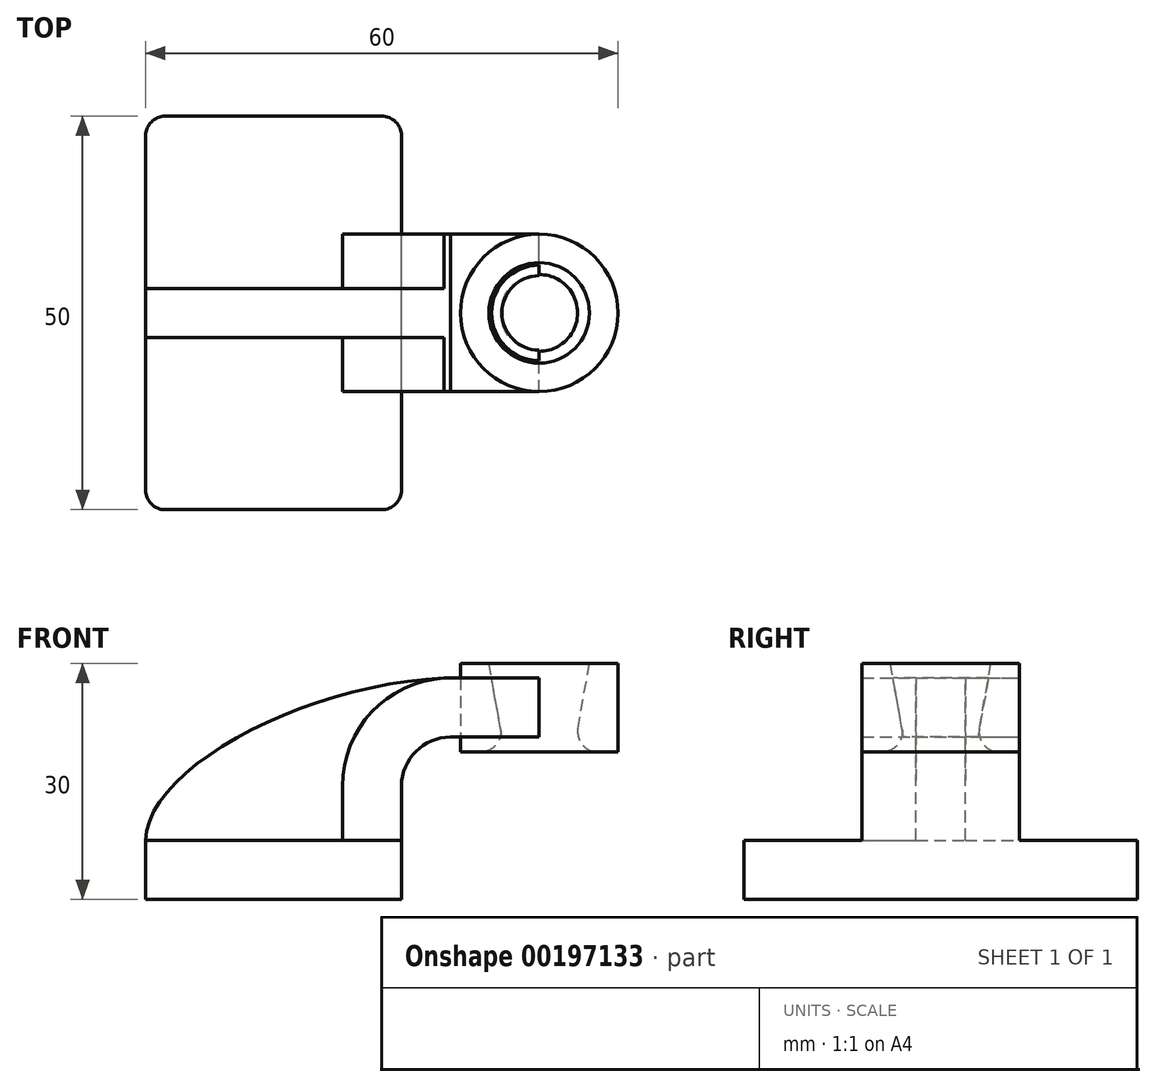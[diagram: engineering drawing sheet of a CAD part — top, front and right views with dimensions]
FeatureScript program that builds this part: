
annotation { "Feature Type Name" : "Feature", "Feature Type Description" : "" }
export const myFeature = defineFeature(function(context is Context, id is Id, definition is map)
    precondition{}
    {
        {
            var Q0;
            Q0=qCreatedBy(makeId("Front.planeOp"),FACE);
            var sketch = newSketch(context, id + "F0", { "sketchPlane" : qUnion([Q0])});
            skLineSegment(sketch, "E0.bottom", {"start": v(16.25, 3.75) * mm, "end": v(-16.25, 3.75) * mm});
            skLineSegment(sketch, "E0.top", {"start": v(16.25, -3.75) * mm, "end": v(-16.25, -3.75) * mm});
            skLineSegment(sketch, "E0.left", {"start": v(16.25, 3.75) * mm, "end": v(16.25, -3.75) * mm});
            skLineSegment(sketch, "E0.right", {"start": v(-16.25, 3.75) * mm, "end": v(-16.25, -3.75) * mm});
            skPoint(sketch, "E0.middle", {"position": v(0, 0) * mm});
            skLineSegment(sketch, "E1.bottom", {"start": v(43.75, 15) * mm, "end": v(23.75, 15) * mm});
            skLineSegment(sketch, "E1.top", {"start": v(43.75, 26.25) * mm, "end": v(23.75, 26.25) * mm});
            skLineSegment(sketch, "E1.left", {"start": v(43.75, 15) * mm, "end": v(43.75, 26.25) * mm});
            skLineSegment(sketch, "E1.right", {"start": v(23.75, 15) * mm, "end": v(23.75, 26.25) * mm});
            skPoint(sketch, "E1.middle", {"position": v(33.75, 20.63) * mm});
            skLineSegment(sketch, "E2", {"start": v(16.25, 3.75) * mm, "end": v(16.25, 10.63) * mm});
            skArc(sketch, "E3", {"start": v(16.25, 10.63) * mm, "mid": v(18.08, 15.05) * mm, "end": v(22.5, 16.88) * mm});
            skLineSegment(sketch, "E4", {"start": v(22.5, 16.88) * mm, "end": v(33.75, 16.88) * mm});
            skLineSegment(sketch, "E5.0", {"start": v(22.5, 24.38) * mm, "end": v(33.75, 24.38) * mm});
            skArc(sketch, "E5.1", {"start": v(8.75, 10.63) * mm, "mid": v(12.78, 20.35) * mm, "end": v(22.5, 24.38) * mm});
            skLineSegment(sketch, "E5.2", {"start": v(8.75, 3.75) * mm, "end": v(8.75, 10.63) * mm});
            skLineSegment(sketch, "E6", {"start": v(33.75, 15) * mm, "end": v(33.75, 26.25) * mm});
            skFitSpline(sketch, "E7", {"points": [v(-16.25, 3.75) * mm, v(22.5, 24.38) * mm], "startDerivative": vector(0.42, 28.18) * mm, "endDerivative": vector(52.82, 1.15) * mm});
            skSolve(sketch);
        }
        {
            var Q0;
            Q0=makeQuery(id+"F0.imprint","IMPRINT",FACE,{"disambiguationData":[TD([[makeQuery(id+"F0.imprint","IMPRINT",EDGE,{"derivedFrom":sQuery(id+"F0.wireOp",EDGE,"E0.top")}),-1.0]])]});
            extrude(context, id + "F1", {"entities" : qUnion([Q0]), "endBound" : BoundingType.SYMMETRIC, "depth" : 50 * mm});
        }
        {
            var Q0;
            {var subQ1=sQuery(id+"F0.wireOp",EDGE,"E2");Q0=makeQuery(id+"F0.imprint","IMPRINT",FACE,{"disambiguationData":[TD([[makeQuery(id+"F0.imprint","IMPRINT",EDGE,{"derivedFrom":subQ1}),1.0]])]});}
            var Q1;
            {var subQ0=sQuery(id+"F0.wireOp",EDGE,"E4");var subQ1=sQuery(id+"F0.wireOp",EDGE,"E1.right");var subQ2=makeQuery(id+"F0.imprint","INTERSECT",VERTEX,{"derivedFrom":[subQ1,subQ0]});Q1=makeQuery(id+"F0.imprint","IMPRINT",FACE,{"disambiguationData":[TD([[makeQuery(id+"F0.imprint","IMPRINT",EDGE,{"disambiguationData":[TD([[subQ2,-1.0]])],"derivedFrom":subQ1}),-1.0]])]});}
            extrude(context, id + "F2", {"entities" : qUnion([Q0, Q1]), "operationType" : NewBodyOperationType.ADD, "endBound" : BoundingType.SYMMETRIC, "depth" : 20 * mm});
        }
        {
            var Q0;
            {var subQ3=sQuery(id+"F0.wireOp",EDGE,"E5.2");Q0=makeQuery(id+"F0.imprint","IMPRINT",FACE,{"disambiguationData":[TD([[makeQuery(id+"F0.imprint","IMPRINT",EDGE,{"derivedFrom":subQ3}),1.0]])]});}
            extrude(context, id + "F3", {"entities" : qUnion([Q0]), "operationType" : NewBodyOperationType.ADD, "endBound" : BoundingType.SYMMETRIC, "depth" : 6.25 * mm});
        }
        {
            var Q0;
            {var subQ0=sQuery(id+"F0.wireOp",EDGE,"E1.left");Q0=makeQuery(id+"F0.imprint","IMPRINT",FACE,{"disambiguationData":[TD([[makeQuery(id+"F0.imprint","IMPRINT",EDGE,{"derivedFrom":subQ0}),1.0]])]});}
            var Q1;
            Q1=sQuery(id+"F0.wireOp",EDGE,"E6");
            revolve(context, id + "F4", {"entities" : qUnion([Q0]), "axis" : qUnion([Q1]), "revolveType" : RevolveType.FULL});
        }
        {
            var Q0;
            Q0=makeQuery(id+"F1.opExtrude","CAP_EDGE",EDGE,{"disambiguationData":[OSD([sQuery(id+"F0.wireOp",EDGE,"E0.left")])],"isStart":false});
            var Q1;
            Q1=makeQuery(id+"F1.opExtrude","CAP_EDGE",EDGE,{"disambiguationData":[OSD([sQuery(id+"F0.wireOp",EDGE,"E0.right")])],"isStart":false});
            var Q2;
            Q2=makeQuery(id+"F1.opExtrude","CAP_EDGE",EDGE,{"disambiguationData":[OSD([sQuery(id+"F0.wireOp",EDGE,"E0.right")])],"isStart":true});
            var Q3;
            Q3=makeQuery(id+"F1.opExtrude","CAP_EDGE",EDGE,{"disambiguationData":[OSD([sQuery(id+"F0.wireOp",EDGE,"E0.left")])],"isStart":true});
            fillet(context, id + "F5", {"entities" : qUnion([Q0, Q1, Q2, Q3]), "radius" : 2.5 * mm, "tangentPropagation" : true, "allowEdgeOverflow" : false});
        }
        {
            var Q0;
            Q0=makeQuery(id+"F4.opRevolve","SWEPT_FACE",FACE,{"disambiguationData":[OSD([sQuery(id+"F0.wireOp",EDGE,"E1.top")])]});
            var sketch = newSketch(context, id + "F6", { "sketchPlane" : qUnion([Q0])});
            skCircle(sketch, "E8", {"center": v(33.75, 0) * mm, "radius": 6.38 * mm});
            skSolve(sketch);
        }
        {
            var Q0;
            Q0 = qSketchRegion(id + "F6", true);
            extrude(context, id + "F7", {"entities" : qUnion([Q0]), "operationType" : NewBodyOperationType.REMOVE, "endBound" : BoundingType.THROUGH_ALL, "oppositeDirection" : true, "depth" : 25 * mm, "hasDraft" : true, "draftAngle" : 10 * degree, "draftPullDirection" : true, "hasSecondDirectionDraft" : true, "secondDirectionDraftAngle" : 10 * degree});
        }
        {
            var Q0;
            Q0=makeQuery(id+"F7.boolean.opBoolean","COPY",EDGE,{"derivedFrom":makeQuery(id+"F7.opExtrude","CAP_EDGE",EDGE,{"disambiguationData":[OSD([sQuery(id+"F6.wireOp",EDGE,"E8")])],"isStart":true})});
            var Q1;
            Q1=makeQuery(id+"F7.boolean.opBoolean","INTERSECT",EDGE,{"derivedFrom":[makeQuery(id+"F4.opRevolve","SWEPT_FACE",FACE,{"disambiguationData":[OSD([sQuery(id+"F0.wireOp",EDGE,"E1.bottom")])]}),makeQuery(id+"F7.opExtrude","SWEPT_FACE",FACE,{"disambiguationData":[OSD([sQuery(id+"F6.wireOp",EDGE,"E8")])]})]});
            fillet(context, id + "F8", {"entities" : qUnion([Q0, Q1]), "radius" : 2.5 * mm, "tangentPropagation" : true, "allowEdgeOverflow" : false});
        }
    });
